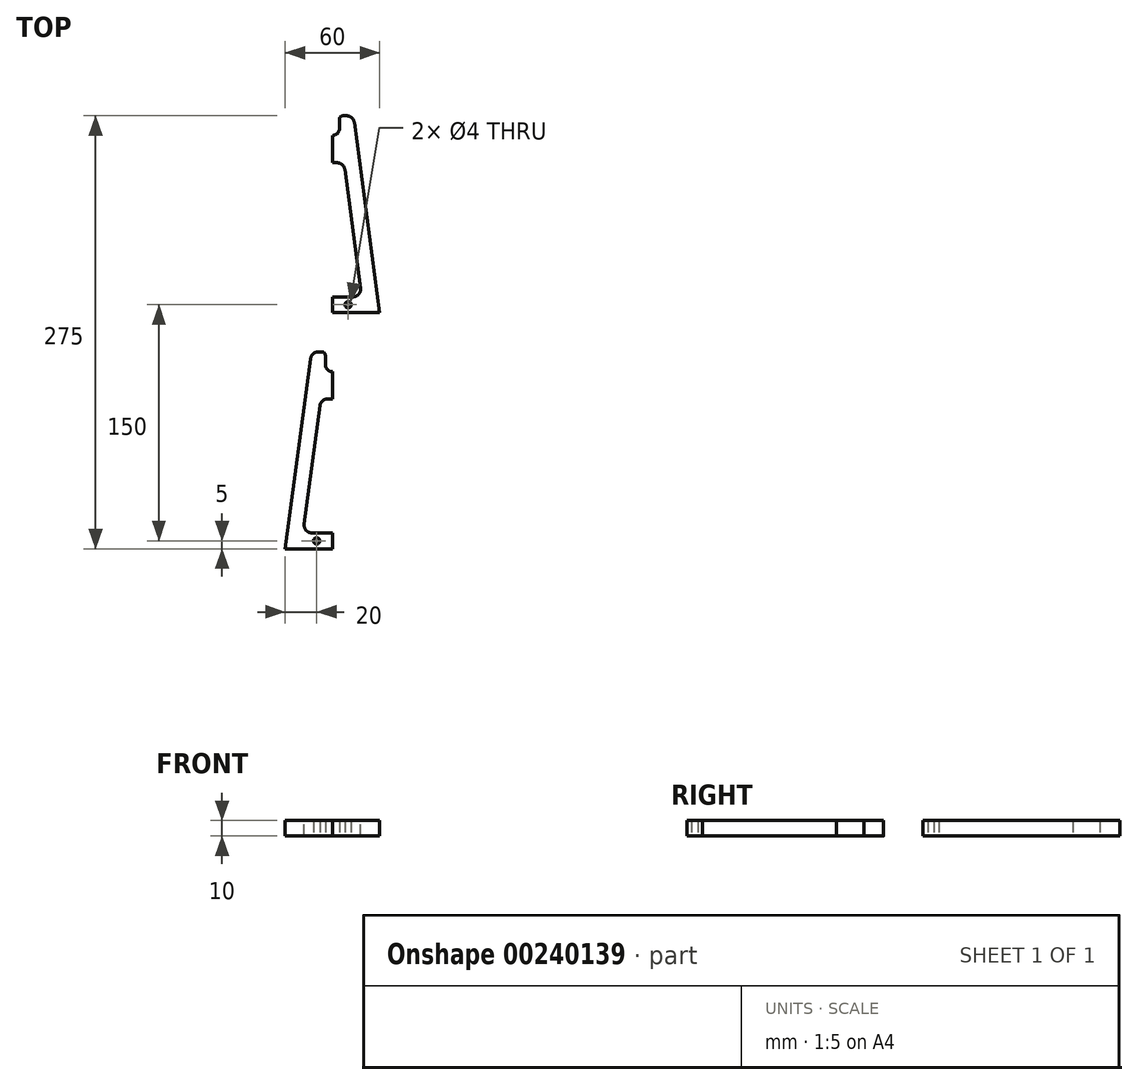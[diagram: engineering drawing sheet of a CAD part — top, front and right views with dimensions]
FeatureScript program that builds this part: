
annotation { "Feature Type Name" : "Feature", "Feature Type Description" : "" }
export const myFeature = defineFeature(function(context is Context, id is Id, definition is map)
    precondition{}
    {
        {
            var Q0;
            Q0=qCreatedBy(makeId("Top.planeOp"),FACE);
            var sketch = newSketch(context, id + "F0", { "sketchPlane" : qUnion([Q0])});
            skLineSegment(sketch, "E0.top", {"start": v(0, 75) * mm, "end": v(-30, 75) * mm});
            skPoint(sketch, "E0.middle", {"position": v(0, 0) * mm});
            skLineSegment(sketch, "E1", {"start": v(-30, 75) * mm, "end": v(-50, -75) * mm});
            skPoint(sketch, "E0.right.end.orphan", {"position": v(-50, 75) * mm});
            skPoint(sketch, "E0.left.end.orphan", {"position": v(50, 75) * mm});
            skLineSegment(sketch, "E2", {"start": v(0, 0) * mm, "end": v(0, 6) * mm});
            skLineSegment(sketch, "E3", {"start": v(-50, -75) * mm, "end": v(-40, -75) * mm});
            skLineSegment(sketch, "E4", {"start": v(-30, 75) * mm, "end": v(-20, 75) * mm});
            skLineSegment(sketch, "E5", {"start": v(0, 75) * mm, "end": v(0, 65) * mm});
            skLineSegment(sketch, "E6", {"start": v(0, 65) * mm, "end": v(-21.33, 65) * mm});
            skLineSegment(sketch, "E7", {"start": v(0, -75) * mm, "end": v(0, -65) * mm});
            skLineSegment(sketch, "E8", {"start": v(0, -65) * mm, "end": v(-38.67, -65) * mm});
            skLineSegment(sketch, "E9", {"start": v(0, 6) * mm, "end": v(-29.2, 6) * mm});
            skLineSegment(sketch, "E10", {"start": v(0, 0) * mm, "end": v(0, -6) * mm});
            skLineSegment(sketch, "E11", {"start": v(0, -6) * mm, "end": v(-30.8, -6) * mm});
            skLineSegment(sketch, "E12.trimOffspring", {"start": v(-30.8, -6) * mm, "end": v(-38.67, -65) * mm});
            skLineSegment(sketch, "E13", {"start": v(-21.33, 65) * mm, "end": v(-29.2, 6) * mm});
            skLineSegment(sketch, "E14.trimOffspring", {"start": v(0, -75) * mm, "end": v(-50, -75) * mm});
            skPoint(sketch, "E0.bottom.start.orphan", {"position": v(50, -75) * mm});
            skCircle(sketch, "E15", {"center": v(-15, 0) * mm, "radius": 2 * mm});
            skLineSegment(sketch, "E16", {"start": v(0, 65) * mm, "end": v(0, 70) * mm});
            skCircle(sketch, "E17", {"center": v(-10.41, 70) * mm, "radius": 2 * mm});
            skSolve(sketch);
        }
        {
            var Q0;
            Q0=qSketchRegion(id+"F0",true);
            extrude(context, id + "F1", {"entities" : qUnion([Q0]), "depth" : 10 * mm});
        }
        {
            var Q0;
            Q0=makeQuery(id+"F1.opExtrude","SWEPT_EDGE",EDGE,{"disambiguationData":[OSD([sQuery(id+"F0.wireOp",EDGE,"E6"),sQuery(id+"F0.wireOp",EDGE,"E13")])]});
            var Q1;
            Q1=makeQuery(id+"F1.opExtrude","SWEPT_EDGE",EDGE,{"disambiguationData":[OSD([sQuery(id+"F0.wireOp",EDGE,"E11"),sQuery(id+"F0.wireOp",EDGE,"E12.trimOffspring")])]});
            var Q2;
            Q2=makeQuery(id+"F1.opExtrude","SWEPT_EDGE",EDGE,{"disambiguationData":[OSD([sQuery(id+"F0.wireOp",EDGE,"E9"),sQuery(id+"F0.wireOp",EDGE,"E13")])]});
            var Q3;
            Q3=makeQuery(id+"F1.opExtrude","SWEPT_EDGE",EDGE,{"disambiguationData":[OSD([sQuery(id+"F0.wireOp",EDGE,"E8"),sQuery(id+"F0.wireOp",EDGE,"E12.trimOffspring")])]});
            var Q4;
            Q4=makeQuery(id+"F1.opExtrude","SWEPT_EDGE",EDGE,{"disambiguationData":[OSD([sQuery(id+"F0.wireOp",EDGE,"E1"),sQuery(id+"F0.wireOp",EDGE,"E14.trimOffspring")])]});
            fillet(context, id + "F2", {"entities" : qUnion([Q0, Q1, Q2, Q3, Q4]), "radius" : 5 * mm, "tangentPropagation" : true, "allowEdgeOverflow" : false});
        }
        {
            var Q0;
            Q0=makeQuery(id+"F1.opExtrude","SWEPT_BODY",BODY,{"disambiguationData":[OSD([sQuery(id+"F0.wireOp",EDGE,"E0.top"),sQuery(id+"F0.wireOp",EDGE,"E1"),sQuery(id+"F0.wireOp",EDGE,"E2"),sQuery(id+"F0.wireOp",EDGE,"E4"),sQuery(id+"F0.wireOp",EDGE,"E5"),sQuery(id+"F0.wireOp",EDGE,"E6"),sQuery(id+"F0.wireOp",EDGE,"E7"),sQuery(id+"F0.wireOp",EDGE,"E8"),sQuery(id+"F0.wireOp",EDGE,"E9"),sQuery(id+"F0.wireOp",EDGE,"E10"),sQuery(id+"F0.wireOp",EDGE,"E11"),sQuery(id+"F0.wireOp",EDGE,"E12.trimOffspring"),sQuery(id+"F0.wireOp",EDGE,"E13"),sQuery(id+"F0.wireOp",EDGE,"E14.trimOffspring"),sQuery(id+"F0.wireOp",EDGE,"E15"),sQuery(id+"F0.wireOp",EDGE,"E16"),sQuery(id+"F0.wireOp",EDGE,"E17")])]});
            var Q1;
            Q1=qCreatedBy(makeId("Right.planeOp"),FACE);
            mirror(context, id + "F3", {"operationType" : NewBodyOperationType.ADD, "entities" : qUnion([Q0]), "mirrorPlane" : qUnion([Q1])});
        }
        {
            var Q0;
            Q0=qCreatedBy(makeId("Top.planeOp"),FACE);
            var sketch = newSketch(context, id + "F4", { "sketchPlane" : qUnion([Q0])});
            skLineSegment(sketch, "E18", {"start": v(0, 0) * mm, "end": v(40, 0) * mm});
            skLineSegment(sketch, "E19", {"start": v(0, 75) * mm, "end": v(30, 75) * mm});
            skLineSegment(sketch, "E20", {"start": v(0, 75) * mm, "end": v(0, 85) * mm});
            skLineSegment(sketch, "E21", {"start": v(4.5, 200) * mm, "end": v(13.33, 200) * mm});
            skLineSegment(sketch, "E22", {"start": v(30, 75) * mm, "end": v(13.33, 200) * mm});
            skArc(sketch, "E23", {"start": v(0, 187.5) * mm, "mid": v(3.18, 188.82) * mm, "end": v(4.5, 192) * mm});
            skLineSegment(sketch, "E24", {"start": v(4.5, 200) * mm, "end": v(4.5, 192) * mm});
            skLineSegment(sketch, "E25", {"start": v(0, 75) * mm, "end": v(0, 80) * mm});
            skCircle(sketch, "E26", {"center": v(10, 80) * mm, "radius": 2 * mm});
            skLineSegment(sketch, "E27", {"start": v(0, 75) * mm, "end": v(10, 75) * mm});
            skLineSegment(sketch, "E28", {"start": v(10, 85) * mm, "end": v(18.67, 85) * mm});
            skLineSegment(sketch, "E29", {"start": v(18.67, 85) * mm, "end": v(10, 150) * mm});
            skLineSegment(sketch, "E30", {"start": v(10, 85) * mm, "end": v(0, 85) * mm});
            skLineSegment(sketch, "E31", {"start": v(18.67, 85) * mm, "end": v(7.31, 170.17) * mm});
            skLineSegment(sketch, "E32", {"start": v(7.31, 170.17) * mm, "end": v(0, 170.17) * mm});
            skLineSegment(sketch, "E33.trimOffspring", {"start": v(0, 170.17) * mm, "end": v(0, 187.5) * mm});
            skSolve(sketch);
        }
        {
            var Q0;
            Q0=qSketchRegion(id+"F4",true);
            extrude(context, id + "F5", {"entities" : qUnion([Q0]), "depth" : 10 * mm});
        }
        {
            var Q0;
            Q0=makeQuery(id+"F5.opExtrude","SWEPT_BODY",BODY,{"disambiguationData":[OSD([sQuery(id+"F4.wireOp",EDGE,"E19"),sQuery(id+"F4.wireOp",EDGE,"E20"),sQuery(id+"F4.wireOp",EDGE,"E21"),sQuery(id+"F4.wireOp",EDGE,"E22"),sQuery(id+"F4.wireOp",EDGE,"E23"),sQuery(id+"F4.wireOp",EDGE,"E24"),sQuery(id+"F4.wireOp",EDGE,"E25"),sQuery(id+"F4.wireOp",EDGE,"E26"),sQuery(id+"F4.wireOp",EDGE,"E27"),sQuery(id+"F4.wireOp",EDGE,"E28"),sQuery(id+"F4.wireOp",EDGE,"E30"),sQuery(id+"F4.wireOp",EDGE,"E31"),sQuery(id+"F4.wireOp",EDGE,"E32"),sQuery(id+"F4.wireOp",EDGE,"E33.trimOffspring")])]});
            var Q1;
            Q1=qCreatedBy(makeId("Right.planeOp"),FACE);
            mirror(context, id + "F6", {"entities" : qUnion([Q0]), "mirrorPlane" : qUnion([Q1])});
        }
        {
            var Q0;
            Q0=makeQuery(id+"F6.opPattern","COPY",EDGE,{"derivedFrom":makeQuery(id+"F5.opExtrude","SWEPT_EDGE",EDGE,{"disambiguationData":[OSD([sQuery(id+"F4.wireOp",EDGE,"E31"),sQuery(id+"F4.wireOp",EDGE,"E32")])]}),"instanceName":"1"});
            var Q1;
            Q1=makeQuery(id+"F5.opExtrude","SWEPT_EDGE",EDGE,{"disambiguationData":[OSD([sQuery(id+"F4.wireOp",EDGE,"E31"),sQuery(id+"F4.wireOp",EDGE,"E32")])]});
            var Q2;
            Q2=makeQuery(id+"F6.opPattern","COPY",EDGE,{"derivedFrom":makeQuery(id+"F5.opExtrude","SWEPT_EDGE",EDGE,{"disambiguationData":[OSD([sQuery(id+"F4.wireOp",EDGE,"E28"),sQuery(id+"F4.wireOp",EDGE,"E31")])]}),"instanceName":"1"});
            var Q3;
            Q3=makeQuery(id+"F5.opExtrude","SWEPT_EDGE",EDGE,{"disambiguationData":[OSD([sQuery(id+"F4.wireOp",EDGE,"E28"),sQuery(id+"F4.wireOp",EDGE,"E31")])]});
            var Q4;
            Q4=makeQuery(id+"F6.opPattern","COPY",EDGE,{"derivedFrom":makeQuery(id+"F5.opExtrude","SWEPT_EDGE",EDGE,{"disambiguationData":[OSD([sQuery(id+"F4.wireOp",EDGE,"E21"),sQuery(id+"F4.wireOp",EDGE,"E22")])]}),"instanceName":"1"});
            var Q5;
            Q5=makeQuery(id+"F5.opExtrude","SWEPT_EDGE",EDGE,{"disambiguationData":[OSD([sQuery(id+"F4.wireOp",EDGE,"E21"),sQuery(id+"F4.wireOp",EDGE,"E22")])]});
            fillet(context, id + "F7", {"entities" : qUnion([Q0, Q1, Q2, Q3, Q4, Q5]), "radius" : 5 * mm, "tangentPropagation" : true, "allowEdgeOverflow" : false});
        }
        {
            var Q0;
            Q0=makeQuery(id+"F5.opExtrude","SWEPT_EDGE",EDGE,{"disambiguationData":[OSD([sQuery(id+"F4.wireOp",EDGE,"E21"),sQuery(id+"F4.wireOp",EDGE,"E24")])]});
            var Q1;
            Q1=makeQuery(id+"F6.opPattern","COPY",EDGE,{"derivedFrom":makeQuery(id+"F5.opExtrude","SWEPT_EDGE",EDGE,{"disambiguationData":[OSD([sQuery(id+"F4.wireOp",EDGE,"E21"),sQuery(id+"F4.wireOp",EDGE,"E24")])]}),"instanceName":"1"});
            fillet(context, id + "F8", {"entities" : qUnion([Q0, Q1]), "radius" : 2 * mm, "tangentPropagation" : true, "allowEdgeOverflow" : false});
        }
        {
            var Q0;
            Q0=qCreatedBy(makeId("Top.planeOp"),FACE);
            var sketch = newSketch(context, id + "F9", { "sketchPlane" : qUnion([Q0])});
            skLineSegment(sketch, "E34", {"start": v(0, 0) * mm, "end": v(0, 6) * mm});
            skLineSegment(sketch, "E35", {"start": v(0, 6) * mm, "end": v(-6, 6) * mm});
            skLineSegment(sketch, "E36", {"start": v(-6, 6) * mm, "end": v(-6, -6) * mm});
            skLineSegment(sketch, "E37", {"start": v(-6, -6) * mm, "end": v(0, -6) * mm});
            skLineSegment(sketch, "E38", {"start": v(0, -6) * mm, "end": v(0, 0) * mm});
            skSolve(sketch);
        }
        {
            var Q0;
            Q0=qSketchRegion(id+"F9",true);
            extrude(context, id + "F10", {"entities" : qUnion([Q0]), "operationType" : NewBodyOperationType.ADD, "depth" : 25 * mm});
        }
        {
            var Q0;
            Q0=makeQuery(id+"F10.opExtrude","SWEPT_EDGE",EDGE,{"disambiguationData":[OSD([sQuery(id+"F9.wireOp",EDGE,"E36"),sQuery(id+"F9.wireOp",EDGE,"E37")])]});
            var Q1;
            Q1=makeQuery(id+"F10.opExtrude","CAP_EDGE",EDGE,{"disambiguationData":[OSD([sQuery(id+"F9.wireOp",EDGE,"E36")])],"isStart":false});
            var Q2;
            Q2=makeQuery(id+"F10.opExtrude","CAP_EDGE",EDGE,{"disambiguationData":[OSD([sQuery(id+"F9.wireOp",EDGE,"E37")])],"isStart":false});
            var Q3;
            Q3=makeQuery(id+"F10.opExtrude","SWEPT_EDGE",EDGE,{"disambiguationData":[OSD([sQuery(id+"F9.wireOp",EDGE,"E35"),sQuery(id+"F9.wireOp",EDGE,"E36")])]});
            var Q4;
            Q4=makeQuery(id+"F10.opExtrude","CAP_EDGE",EDGE,{"disambiguationData":[OSD([sQuery(id+"F9.wireOp",EDGE,"E35")])],"isStart":false});
            fillet(context, id + "F11", {"entities" : qUnion([Q0, Q1, Q2, Q3, Q4]), "radius" : 1.5 * mm, "tangentPropagation" : true, "allowEdgeOverflow" : false});
        }
        {
            var Q0;
            Q0=qCreatedBy(makeId("Right.planeOp"),FACE);
            var sketch = newSketch(context, id + "F12", { "sketchPlane" : qUnion([Q0])});
            skCircle(sketch, "E39", {"center": v(0, 20) * mm, "radius": 1.75 * mm});
            skCircle(sketch, "E40", {"center": v(0, 15) * mm, "radius": 1.75 * mm});
            skSolve(sketch);
        }
        {
            var Q0;
            Q0=qSketchRegion(id+"F12",true);
            extrude(context, id + "F13", {"entities" : qUnion([Q0]), "endBound" : BoundingType.SYMMETRIC, "depth" : 25 * mm});
        }
        {
            var Q0;
            Q0=makeQuery(id+"F13.opExtrude","SWEPT_BODY",BODY,{"disambiguationData":[OSD([sQuery(id+"F12.wireOp",EDGE,"E40")])]});
            var Q1;
            Q1=makeQuery(id+"F13.opExtrude","SWEPT_BODY",BODY,{"disambiguationData":[OSD([sQuery(id+"F12.wireOp",EDGE,"E39")])]});
            var Q2;
            Q2=makeQuery(id+"F1.opExtrude","SWEPT_BODY",BODY,{"disambiguationData":[OSD([sQuery(id+"F0.wireOp",EDGE,"E0.top"),sQuery(id+"F0.wireOp",EDGE,"E1"),sQuery(id+"F0.wireOp",EDGE,"E2"),sQuery(id+"F0.wireOp",EDGE,"E4"),sQuery(id+"F0.wireOp",EDGE,"E5"),sQuery(id+"F0.wireOp",EDGE,"E6"),sQuery(id+"F0.wireOp",EDGE,"E7"),sQuery(id+"F0.wireOp",EDGE,"E8"),sQuery(id+"F0.wireOp",EDGE,"E9"),sQuery(id+"F0.wireOp",EDGE,"E10"),sQuery(id+"F0.wireOp",EDGE,"E11"),sQuery(id+"F0.wireOp",EDGE,"E12.trimOffspring"),sQuery(id+"F0.wireOp",EDGE,"E13"),sQuery(id+"F0.wireOp",EDGE,"E14.trimOffspring"),sQuery(id+"F0.wireOp",EDGE,"E15"),sQuery(id+"F0.wireOp",EDGE,"E16"),sQuery(id+"F0.wireOp",EDGE,"E17")])]});
            booleanBodies(context, id + "F14", {"operationType" : BooleanOperationType.SUBTRACTION, "tools" : qUnion([Q0, Q1]), "targets" : qUnion([Q2])});
        }
        {
            var Q0;
            Q0=qCreatedBy(makeId("Top.planeOp"),FACE);
            var sketch = newSketch(context, id + "F15", { "sketchPlane" : qUnion([Q0])});
            skLineSegment(sketch, "E41.bottom", {"start": v(15, 65) * mm, "end": v(-15, 65) * mm});
            skLineSegment(sketch, "E41.top", {"start": v(15, 85) * mm, "end": v(-15, 85) * mm});
            skLineSegment(sketch, "E41.left", {"start": v(15, 65) * mm, "end": v(15, 85) * mm});
            skLineSegment(sketch, "E41.right", {"start": v(-15, 65) * mm, "end": v(-15, 85) * mm});
            skPoint(sketch, "E41.middle", {"position": v(0, 75) * mm});
            skLineSegment(sketch, "E42", {"start": v(0, 75) * mm, "end": v(0, 85) * mm});
            skLineSegment(sketch, "E43", {"start": v(0, 85) * mm, "end": v(0, 65) * mm});
            skLineSegment(sketch, "E44", {"start": v(0, 65) * mm, "end": v(-6, 65) * mm});
            skLineSegment(sketch, "E45", {"start": v(-6, 65) * mm, "end": v(-6, 85) * mm});
            skLineSegment(sketch, "E46", {"start": v(-6, 85) * mm, "end": v(0, 85) * mm});
            skSolve(sketch);
        }
        {
            var Q0;
            Q0=qSketchRegion(id+"F15",true);
            extrude(context, id + "F16", {"entities" : qUnion([Q0]), "depth" : 10 * mm});
        }
        {
            var Q0;
            Q0=qCreatedBy(makeId("Top.planeOp"),FACE);
            var sketch = newSketch(context, id + "F17", { "sketchPlane" : qUnion([Q0])});
            skLineSegment(sketch, "E47", {"start": v(0, 65) * mm, "end": v(0, 85) * mm});
            skLineSegment(sketch, "E48", {"start": v(0, 85) * mm, "end": v(-6, 85) * mm});
            skLineSegment(sketch, "E49", {"start": v(-6, 85) * mm, "end": v(-6, 65) * mm});
            skLineSegment(sketch, "E50", {"start": v(-6, 65) * mm, "end": v(0, 65) * mm});
            skSolve(sketch);
        }
        {
            var Q0;
            Q0=qSketchRegion(id+"F17",true);
            extrude(context, id + "F18", {"entities" : qUnion([Q0]), "depth" : 25 * mm});
        }
        {
            var Q0;
            Q0=makeQuery(id+"F16.opExtrude","SWEPT_BODY",BODY,{"disambiguationData":[OSD([sQuery(id+"F15.wireOp",EDGE,"E41.bottom"),sQuery(id+"F15.wireOp",EDGE,"E41.top"),sQuery(id+"F15.wireOp",EDGE,"E41.left"),sQuery(id+"F15.wireOp",EDGE,"E41.right"),sQuery(id+"F15.wireOp",EDGE,"E44"),sQuery(id+"F15.wireOp",EDGE,"E46")])]});
            var Q1;
            Q1=makeQuery(id+"F18.opExtrude","SWEPT_BODY",BODY,{"disambiguationData":[OSD([sQuery(id+"F17.wireOp",EDGE,"E47"),sQuery(id+"F17.wireOp",EDGE,"E48"),sQuery(id+"F17.wireOp",EDGE,"E49"),sQuery(id+"F17.wireOp",EDGE,"E50")])]});
            booleanBodies(context, id + "F19", {"operationType" : BooleanOperationType.UNION, "tools" : qUnion([Q0, Q1])});
        }
        {
            var Q0;
            Q0=makeQuery(id+"F16.opExtrude","SWEPT_BODY",BODY,{"disambiguationData":[OSD([sQuery(id+"F15.wireOp",EDGE,"E41.bottom"),sQuery(id+"F15.wireOp",EDGE,"E41.top"),sQuery(id+"F15.wireOp",EDGE,"E41.left"),sQuery(id+"F15.wireOp",EDGE,"E41.right"),sQuery(id+"F15.wireOp",EDGE,"E44"),sQuery(id+"F15.wireOp",EDGE,"E46")])]});
            transform(context, id + "F20", {"entities" : qUnion([Q0]), "transformType" : TransformType.TRANSLATION_3D, "dx" : 0 * mm, "dy" : 0 * mm, "dz" : 10 * mm, "makeCopy" : false});
        }
        {
            var Q0;
            Q0=qCreatedBy(makeId("Top.planeOp"),FACE);
            var sketch = newSketch(context, id + "F21", { "sketchPlane" : qUnion([Q0])});
            skCircle(sketch, "E51", {"center": v(-10, 80) * mm, "radius": 2 * mm});
            skCircle(sketch, "E52", {"center": v(10, 80) * mm, "radius": 2 * mm});
            skCircle(sketch, "E53", {"center": v(-10.4, 70) * mm, "radius": 2 * mm});
            skCircle(sketch, "E54", {"center": v(10.4, 70) * mm, "radius": 2 * mm});
            skSolve(sketch);
        }
        {
            var Q0;
            Q0=qSketchRegion(id+"F21",true);
            extrude(context, id + "F22", {"entities" : qUnion([Q0]), "depth" : 30 * mm});
        }
        {
            var Q0;
            Q0=makeQuery(id+"F22.opExtrude","SWEPT_BODY",BODY,{"disambiguationData":[OSD([sQuery(id+"F21.wireOp",EDGE,"E54")])]});
            var Q1;
            Q1=makeQuery(id+"F22.opExtrude","SWEPT_BODY",BODY,{"disambiguationData":[OSD([sQuery(id+"F21.wireOp",EDGE,"E53")])]});
            var Q2;
            Q2=makeQuery(id+"F22.opExtrude","SWEPT_BODY",BODY,{"disambiguationData":[OSD([sQuery(id+"F21.wireOp",EDGE,"E52")])]});
            var Q3;
            Q3=makeQuery(id+"F22.opExtrude","SWEPT_BODY",BODY,{"disambiguationData":[OSD([sQuery(id+"F21.wireOp",EDGE,"E51")])]});
            var Q4;
            Q4=makeQuery(id+"F16.opExtrude","SWEPT_BODY",BODY,{"disambiguationData":[OSD([sQuery(id+"F15.wireOp",EDGE,"E41.bottom"),sQuery(id+"F15.wireOp",EDGE,"E41.top"),sQuery(id+"F15.wireOp",EDGE,"E41.left"),sQuery(id+"F15.wireOp",EDGE,"E41.right"),sQuery(id+"F15.wireOp",EDGE,"E44"),sQuery(id+"F15.wireOp",EDGE,"E46")])]});
            booleanBodies(context, id + "F23", {"operationType" : BooleanOperationType.SUBTRACTION, "tools" : qUnion([Q0, Q1, Q2, Q3]), "targets" : qUnion([Q4])});
        }
        {
            var Q0;
            Q0=qCreatedBy(makeId("Right.planeOp"),FACE);
            var sketch = newSketch(context, id + "F24", { "sketchPlane" : qUnion([Q0])});
            skCircle(sketch, "E55", {"center": v(80, 27.23) * mm, "radius": 2 * mm});
            skCircle(sketch, "E56", {"center": v(70, 27.23) * mm, "radius": 2 * mm});
            skSolve(sketch);
        }
        {
            var Q0;
            Q0=qSketchRegion(id+"F24",true);
            extrude(context, id + "F25", {"entities" : qUnion([Q0]), "endBound" : BoundingType.SYMMETRIC, "depth" : 25 * mm});
        }
        {
            var Q0;
            Q0=makeQuery(id+"F25.opExtrude","SWEPT_BODY",BODY,{"disambiguationData":[OSD([sQuery(id+"F24.wireOp",EDGE,"E56")])]});
            var Q1;
            Q1=makeQuery(id+"F25.opExtrude","SWEPT_BODY",BODY,{"disambiguationData":[OSD([sQuery(id+"F24.wireOp",EDGE,"E55")])]});
            var Q2;
            Q2=makeQuery(id+"F16.opExtrude","SWEPT_BODY",BODY,{"disambiguationData":[OSD([sQuery(id+"F15.wireOp",EDGE,"E41.bottom"),sQuery(id+"F15.wireOp",EDGE,"E41.top"),sQuery(id+"F15.wireOp",EDGE,"E41.left"),sQuery(id+"F15.wireOp",EDGE,"E41.right"),sQuery(id+"F15.wireOp",EDGE,"E44"),sQuery(id+"F15.wireOp",EDGE,"E46")])]});
            booleanBodies(context, id + "F26", {"operationType" : BooleanOperationType.SUBTRACTION, "tools" : qUnion([Q0, Q1]), "targets" : qUnion([Q2])});
        }
        {
            var Q0;
            Q0=makeQuery(id+"F18.opExtrude","SWEPT_EDGE",EDGE,{"disambiguationData":[OSD([sQuery(id+"F17.wireOp",EDGE,"E49"),sQuery(id+"F17.wireOp",EDGE,"E50")])]});
            var Q1;
            Q1=makeQuery(id+"F18.opExtrude","CAP_EDGE",EDGE,{"disambiguationData":[OSD([sQuery(id+"F17.wireOp",EDGE,"E50")])],"isStart":false});
            var Q2;
            {var subQ0=sQuery(id+"F15.wireOp",EDGE,"E44");var subQ1=sQuery(id+"F15.wireOp",EDGE,"E41.bottom");var subQ2=sQuery(id+"F15.wireOp",EDGE,"E41.right");Q2=makeQuery(id+"F19.opBoolean","SPLIT",EDGE,{"disambiguationData":[TD([makeQuery(id+"F16.opExtrude","SWEPT_FACE",FACE,{"disambiguationData":[OSD([subQ2])]})])],"derivedFrom":makeQuery(id+"F16.opExtrude","CAP_EDGE",EDGE,{"disambiguationData":[OSD([subQ1,subQ0])],"isStart":false})});}
            var Q3;
            Q3=makeQuery(id+"F16.opExtrude","SWEPT_EDGE",EDGE,{"disambiguationData":[OSD([sQuery(id+"F15.wireOp",EDGE,"E41.bottom"),sQuery(id+"F15.wireOp",EDGE,"E41.right")])]});
            var Q4;
            {var subQ0=sQuery(id+"F15.wireOp",EDGE,"E41.left");var subQ1=sQuery(id+"F15.wireOp",EDGE,"E44");var subQ2=sQuery(id+"F15.wireOp",EDGE,"E41.bottom");Q4=makeQuery(id+"F19.opBoolean","SPLIT",EDGE,{"disambiguationData":[TD([makeQuery(id+"F16.opExtrude","SWEPT_FACE",FACE,{"disambiguationData":[OSD([subQ0])]})])],"derivedFrom":makeQuery(id+"F16.opExtrude","CAP_EDGE",EDGE,{"disambiguationData":[OSD([subQ2,subQ1])],"isStart":false})});}
            var Q5;
            Q5=makeQuery(id+"F16.opExtrude","SWEPT_EDGE",EDGE,{"disambiguationData":[OSD([sQuery(id+"F15.wireOp",EDGE,"E41.bottom"),sQuery(id+"F15.wireOp",EDGE,"E41.left")])]});
            var Q6;
            Q6=makeQuery(id+"F16.opExtrude","CAP_EDGE",EDGE,{"disambiguationData":[OSD([sQuery(id+"F15.wireOp",EDGE,"E41.left")])],"isStart":false});
            var Q7;
            Q7=makeQuery(id+"F16.opExtrude","CAP_EDGE",EDGE,{"disambiguationData":[OSD([sQuery(id+"F15.wireOp",EDGE,"E41.right")])],"isStart":false});
            var Q8;
            Q8=makeQuery(id+"F18.opExtrude","CAP_EDGE",EDGE,{"disambiguationData":[OSD([sQuery(id+"F17.wireOp",EDGE,"E49")])],"isStart":false});
            var Q9;
            {var subQ0=sQuery(id+"F15.wireOp",EDGE,"E41.right");var subQ1=sQuery(id+"F15.wireOp",EDGE,"E46");var subQ2=sQuery(id+"F15.wireOp",EDGE,"E41.top");Q9=makeQuery(id+"F19.opBoolean","SPLIT",EDGE,{"disambiguationData":[TD([makeQuery(id+"F16.opExtrude","SWEPT_FACE",FACE,{"disambiguationData":[OSD([subQ0])]})])],"derivedFrom":makeQuery(id+"F16.opExtrude","CAP_EDGE",EDGE,{"disambiguationData":[OSD([subQ2,subQ1])],"isStart":false})});}
            var Q10;
            Q10=makeQuery(id+"F16.opExtrude","SWEPT_EDGE",EDGE,{"disambiguationData":[OSD([sQuery(id+"F15.wireOp",EDGE,"E41.top"),sQuery(id+"F15.wireOp",EDGE,"E41.right")])]});
            var Q11;
            Q11=makeQuery(id+"F18.opExtrude","SWEPT_EDGE",EDGE,{"disambiguationData":[OSD([sQuery(id+"F17.wireOp",EDGE,"E48"),sQuery(id+"F17.wireOp",EDGE,"E49")])]});
            var Q12;
            Q12=makeQuery(id+"F18.opExtrude","CAP_EDGE",EDGE,{"disambiguationData":[OSD([sQuery(id+"F17.wireOp",EDGE,"E48")])],"isStart":false});
            var Q13;
            {var subQ0=sQuery(id+"F15.wireOp",EDGE,"E41.left");var subQ1=sQuery(id+"F15.wireOp",EDGE,"E46");var subQ2=sQuery(id+"F15.wireOp",EDGE,"E41.top");Q13=makeQuery(id+"F19.opBoolean","SPLIT",EDGE,{"disambiguationData":[TD([makeQuery(id+"F16.opExtrude","SWEPT_FACE",FACE,{"disambiguationData":[OSD([subQ0])]})])],"derivedFrom":makeQuery(id+"F16.opExtrude","CAP_EDGE",EDGE,{"disambiguationData":[OSD([subQ2,subQ1])],"isStart":false})});}
            var Q14;
            Q14=makeQuery(id+"F16.opExtrude","SWEPT_EDGE",EDGE,{"disambiguationData":[OSD([sQuery(id+"F15.wireOp",EDGE,"E41.top"),sQuery(id+"F15.wireOp",EDGE,"E41.left")])]});
            fillet(context, id + "F27", {"entities" : qUnion([Q0, Q1, Q2, Q3, Q4, Q5, Q6, Q7, Q8, Q9, Q10, Q11, Q12, Q13, Q14]), "radius" : 2 * mm, "tangentPropagation" : true, "allowEdgeOverflow" : false});
        }
        {
            var Q0;
            Q0=qCreatedBy(makeId("Right.planeOp"),FACE);
            var sketch = newSketch(context, id + "F28", { "sketchPlane" : qUnion([Q0])});
            skLineSegment(sketch, "E57", {"start": v(0, 0) * mm, "end": v(0, 10) * mm});
            skLineSegment(sketch, "E58", {"start": v(0, 10) * mm, "end": v(6, 10) * mm});
            skLineSegment(sketch, "E59", {"start": v(6, 10) * mm, "end": v(6, 25) * mm});
            skLineSegment(sketch, "E60", {"start": v(-6, 25) * mm, "end": v(-6, 10) * mm});
            skLineSegment(sketch, "E61", {"start": v(-6, 10) * mm, "end": v(0, 10) * mm});
            skLineSegment(sketch, "E62", {"start": v(75, 10) * mm, "end": v(75, 20) * mm});
            skLineSegment(sketch, "E63", {"start": v(75, 20) * mm, "end": v(85, 20) * mm});
            skLineSegment(sketch, "E64", {"start": v(85, 20) * mm, "end": v(85, 35) * mm});
            skLineSegment(sketch, "E65", {"start": v(65, 35) * mm, "end": v(65, 20) * mm});
            skLineSegment(sketch, "E66", {"start": v(65, 20) * mm, "end": v(75, 20) * mm});
            skLineSegment(sketch, "E67", {"start": v(-6, 10) * mm, "end": v(-6, 25) * mm});
            skLineSegment(sketch, "E68", {"start": v(75, 120) * mm, "end": v(85, 120) * mm});
            skLineSegment(sketch, "E69", {"start": v(85, 35) * mm, "end": v(85, 120) * mm});
            skLineSegment(sketch, "E70", {"start": v(85, 120) * mm, "end": v(75, 120) * mm});
            skLineSegment(sketch, "E71", {"start": v(6, 25) * mm, "end": v(65, 35) * mm});
            skLineSegment(sketch, "E72", {"start": v(-6, 25) * mm, "end": v(75, 120) * mm});
            skLineSegment(sketch, "E73", {"start": v(23.92, 44.68) * mm, "end": v(75, 104.59) * mm});
            skLineSegment(sketch, "E74", {"start": v(23.92, 44.68) * mm, "end": v(17.44, 37.08) * mm});
            skLineSegment(sketch, "E75", {"start": v(75, 45) * mm, "end": v(64.16, 45) * mm});
            skLineSegment(sketch, "E76", {"start": v(51.92, 42.93) * mm, "end": v(17.44, 37.08) * mm});
            skLineSegment(sketch, "E77", {"start": v(51.92, 42.93) * mm, "end": v(64.16, 45) * mm});
            skPoint(sketch, "E78.orphan", {"position": v(75, 35) * mm});
            skPoint(sketch, "E79.start.orphan", {"position": v(75, 110) * mm});
            skLineSegment(sketch, "E80", {"start": v(75, 104.59) * mm, "end": v(75, 45) * mm});
            skCircle(sketch, "E81", {"center": v(80, 110) * mm, "radius": 2 * mm});
            skCircle(sketch, "E82", {"center": v(80, 95) * mm, "radius": 2 * mm});
            skPoint(sketch, "E83.end.orphan", {"position": v(80, 120) * mm});
            skSolve(sketch);
        }
        {
            var Q0;
            Q0=qSketchRegion(id+"F28",true);
            extrude(context, id + "F29", {"entities" : qUnion([Q0]), "depth" : 8 * mm});
        }
        {
            var Q0;
            Q0=makeQuery(id+"F29.opExtrude","SWEPT_EDGE",EDGE,{"disambiguationData":[OSD([sQuery(id+"F28.wireOp",EDGE,"E73"),sQuery(id+"F28.wireOp",EDGE,"E80")])]});
            var Q1;
            Q1=makeQuery(id+"F29.opExtrude","SWEPT_EDGE",EDGE,{"disambiguationData":[OSD([sQuery(id+"F28.wireOp",EDGE,"E75"),sQuery(id+"F28.wireOp",EDGE,"E80")])]});
            var Q2;
            Q2=makeQuery(id+"F29.opExtrude","SWEPT_EDGE",EDGE,{"disambiguationData":[OSD([sQuery(id+"F28.wireOp",EDGE,"E74"),sQuery(id+"F28.wireOp",EDGE,"E76")])]});
            var Q3;
            Q3=makeQuery(id+"F29.opExtrude","SWEPT_EDGE",EDGE,{"disambiguationData":[OSD([sQuery(id+"F28.wireOp",EDGE,"E65"),sQuery(id+"F28.wireOp",EDGE,"E71")])]});
            var Q4;
            Q4=makeQuery(id+"F29.opExtrude","SWEPT_EDGE",EDGE,{"disambiguationData":[OSD([sQuery(id+"F28.wireOp",EDGE,"E59"),sQuery(id+"F28.wireOp",EDGE,"E71")])]});
            var Q5;
            Q5=makeQuery(id+"F29.opExtrude","SWEPT_EDGE",EDGE,{"disambiguationData":[OSD([sQuery(id+"F28.wireOp",EDGE,"E67"),sQuery(id+"F28.wireOp",EDGE,"E72")])]});
            fillet(context, id + "F30", {"entities" : qUnion([Q0, Q1, Q2, Q3, Q4, Q5]), "radius" : 2 * mm, "tangentPropagation" : true, "allowEdgeOverflow" : false});
        }
        {
            var Q0;
            Q0=makeQuery(id+"F29.opExtrude","CAP_EDGE",EDGE,{"disambiguationData":[OSD([sQuery(id+"F28.wireOp",EDGE,"E73"),sQuery(id+"F28.wireOp",EDGE,"E74")])],"isStart":false});
            var Q1;
            Q1=makeQuery(id+"F29.opExtrude","CAP_EDGE",EDGE,{"disambiguationData":[OSD([sQuery(id+"F28.wireOp",EDGE,"E72")])],"isStart":false});
            var Q2;
            Q2=makeQuery(id+"F29.opExtrude","CAP_EDGE",EDGE,{"disambiguationData":[OSD([sQuery(id+"F28.wireOp",EDGE,"E71")])],"isStart":false});
            var Q3;
            Q3=makeQuery(id+"F29.opExtrude","CAP_EDGE",EDGE,{"disambiguationData":[OSD([sQuery(id+"F28.wireOp",EDGE,"E64"),sQuery(id+"F28.wireOp",EDGE,"E69")])],"isStart":false});
            fillet(context, id + "F31", {"entities" : qUnion([Q0, Q1, Q2, Q3]), "radius" : 2 * mm, "tangentPropagation" : true, "allowEdgeOverflow" : false});
        }
        {
            var Q0;
            Q0=qCreatedBy(makeId("Right.planeOp"),FACE);
            var sketch = newSketch(context, id + "F32", { "sketchPlane" : qUnion([Q0])});
            skCircle(sketch, "E84", {"center": v(0, 20) * mm, "radius": 1.75 * mm});
            skCircle(sketch, "E85", {"center": v(0, 15) * mm, "radius": 1.75 * mm});
            skCircle(sketch, "E86", {"center": v(70, 27.25) * mm, "radius": 2 * mm});
            skCircle(sketch, "E87", {"center": v(80, 27.25) * mm, "radius": 2 * mm});
            skSolve(sketch);
        }
        {
            var Q0;
            Q0=qSketchRegion(id+"F32",true);
            extrude(context, id + "F33", {"entities" : qUnion([Q0]), "depth" : 25 * mm});
        }
        {
            var Q0;
            Q0=makeQuery(id+"F33.opExtrude","SWEPT_BODY",BODY,{"disambiguationData":[OSD([sQuery(id+"F32.wireOp",EDGE,"E87")])]});
            var Q1;
            Q1=makeQuery(id+"F33.opExtrude","SWEPT_BODY",BODY,{"disambiguationData":[OSD([sQuery(id+"F32.wireOp",EDGE,"E86")])]});
            var Q2;
            Q2=makeQuery(id+"F33.opExtrude","SWEPT_BODY",BODY,{"disambiguationData":[OSD([sQuery(id+"F32.wireOp",EDGE,"E85")])]});
            var Q3;
            Q3=makeQuery(id+"F33.opExtrude","SWEPT_BODY",BODY,{"disambiguationData":[OSD([sQuery(id+"F32.wireOp",EDGE,"E84")])]});
            var Q4;
            Q4=makeQuery(id+"F29.opExtrude","SWEPT_BODY",BODY,{"disambiguationData":[OSD([sQuery(id+"F28.wireOp",EDGE,"E59"),sQuery(id+"F28.wireOp",EDGE,"E61"),sQuery(id+"F28.wireOp",EDGE,"E58"),sQuery(id+"F28.wireOp",EDGE,"E63"),sQuery(id+"F28.wireOp",EDGE,"E64"),sQuery(id+"F28.wireOp",EDGE,"E65"),sQuery(id+"F28.wireOp",EDGE,"E66"),sQuery(id+"F28.wireOp",EDGE,"E67"),sQuery(id+"F28.wireOp",EDGE,"E69"),sQuery(id+"F28.wireOp",EDGE,"E70"),sQuery(id+"F28.wireOp",EDGE,"E71"),sQuery(id+"F28.wireOp",EDGE,"E72"),sQuery(id+"F28.wireOp",EDGE,"E73"),sQuery(id+"F28.wireOp",EDGE,"E74"),sQuery(id+"F28.wireOp",EDGE,"E75"),sQuery(id+"F28.wireOp",EDGE,"E76"),sQuery(id+"F28.wireOp",EDGE,"E77"),sQuery(id+"F28.wireOp",EDGE,"E80"),sQuery(id+"F28.wireOp",EDGE,"E81"),sQuery(id+"F28.wireOp",EDGE,"E82")])]});
            booleanBodies(context, id + "F34", {"operationType" : BooleanOperationType.SUBTRACTION, "tools" : qUnion([Q0, Q1, Q2, Q3]), "targets" : qUnion([Q4])});
        }
        {
            var Q0;
            Q0=makeQuery(id+"F16.opExtrude","SWEPT_BODY",BODY,{"disambiguationData":[OSD([sQuery(id+"F15.wireOp",EDGE,"E41.bottom"),sQuery(id+"F15.wireOp",EDGE,"E41.top"),sQuery(id+"F15.wireOp",EDGE,"E41.left"),sQuery(id+"F15.wireOp",EDGE,"E41.right"),sQuery(id+"F15.wireOp",EDGE,"E44"),sQuery(id+"F15.wireOp",EDGE,"E46")])]});
            var Q1;
            Q1=makeQuery(id+"F29.opExtrude","SWEPT_BODY",BODY,{"disambiguationData":[OSD([sQuery(id+"F28.wireOp",EDGE,"E59"),sQuery(id+"F28.wireOp",EDGE,"E61"),sQuery(id+"F28.wireOp",EDGE,"E58"),sQuery(id+"F28.wireOp",EDGE,"E63"),sQuery(id+"F28.wireOp",EDGE,"E64"),sQuery(id+"F28.wireOp",EDGE,"E65"),sQuery(id+"F28.wireOp",EDGE,"E66"),sQuery(id+"F28.wireOp",EDGE,"E67"),sQuery(id+"F28.wireOp",EDGE,"E69"),sQuery(id+"F28.wireOp",EDGE,"E70"),sQuery(id+"F28.wireOp",EDGE,"E71"),sQuery(id+"F28.wireOp",EDGE,"E72"),sQuery(id+"F28.wireOp",EDGE,"E73"),sQuery(id+"F28.wireOp",EDGE,"E74"),sQuery(id+"F28.wireOp",EDGE,"E75"),sQuery(id+"F28.wireOp",EDGE,"E76"),sQuery(id+"F28.wireOp",EDGE,"E77"),sQuery(id+"F28.wireOp",EDGE,"E80"),sQuery(id+"F28.wireOp",EDGE,"E81"),sQuery(id+"F28.wireOp",EDGE,"E82")])]});
            var Q2;
            Q2=makeQuery(id+"F1.opExtrude","SWEPT_BODY",BODY,{"disambiguationData":[OSD([sQuery(id+"F0.wireOp",EDGE,"E0.top"),sQuery(id+"F0.wireOp",EDGE,"E1"),sQuery(id+"F0.wireOp",EDGE,"E2"),sQuery(id+"F0.wireOp",EDGE,"E4"),sQuery(id+"F0.wireOp",EDGE,"E5"),sQuery(id+"F0.wireOp",EDGE,"E6"),sQuery(id+"F0.wireOp",EDGE,"E7"),sQuery(id+"F0.wireOp",EDGE,"E8"),sQuery(id+"F0.wireOp",EDGE,"E9"),sQuery(id+"F0.wireOp",EDGE,"E10"),sQuery(id+"F0.wireOp",EDGE,"E11"),sQuery(id+"F0.wireOp",EDGE,"E12.trimOffspring"),sQuery(id+"F0.wireOp",EDGE,"E13"),sQuery(id+"F0.wireOp",EDGE,"E14.trimOffspring"),sQuery(id+"F0.wireOp",EDGE,"E15"),sQuery(id+"F0.wireOp",EDGE,"E16"),sQuery(id+"F0.wireOp",EDGE,"E17")])]});
            deleteBodies(context, id + "F35", {"entities" : qUnion([Q0, Q1, Q2])});
        }
        {
            var Q0;
            Q0=makeQuery(id+"F6.opPattern","COPY",BODY,{"derivedFrom":makeQuery(id+"F5.opExtrude","SWEPT_BODY",BODY,{"disambiguationData":[OSD([sQuery(id+"F4.wireOp",EDGE,"E19"),sQuery(id+"F4.wireOp",EDGE,"E20"),sQuery(id+"F4.wireOp",EDGE,"E21"),sQuery(id+"F4.wireOp",EDGE,"E22"),sQuery(id+"F4.wireOp",EDGE,"E23"),sQuery(id+"F4.wireOp",EDGE,"E24"),sQuery(id+"F4.wireOp",EDGE,"E25"),sQuery(id+"F4.wireOp",EDGE,"E26"),sQuery(id+"F4.wireOp",EDGE,"E27"),sQuery(id+"F4.wireOp",EDGE,"E28"),sQuery(id+"F4.wireOp",EDGE,"E30"),sQuery(id+"F4.wireOp",EDGE,"E31"),sQuery(id+"F4.wireOp",EDGE,"E32"),sQuery(id+"F4.wireOp",EDGE,"E33.trimOffspring")])]}),"instanceName":"1"});
            transform(context, id + "F36", {"entities" : qUnion([Q0]), "transformType" : TransformType.TRANSLATION_3D, "dx" : 0 * mm, "dy" : -150 * mm, "dz" : 0 * mm, "makeCopy" : false});
        }
    });
